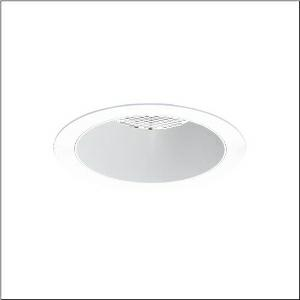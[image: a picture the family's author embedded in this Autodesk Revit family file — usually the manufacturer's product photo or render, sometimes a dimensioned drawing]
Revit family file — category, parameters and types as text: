
# Revit family: lunis_21_xl_51db18mf91c
name_source: partatom
category: Lighting Fixtures
units: mm (PartAtom-declared; Revit-internal decimal feet)

## family parameters
Cut with Voids When Loaded = No
Host = Face
Light Source = No
Part Type = Normal
Room Calculation Point = No
Round Connector Dimension = Use Diameter
Shared = No

## types (1)
- --- (1 x LED, 3700 lm, 21.7 W, 6500K)
    Apparent Load = 22 VA
    CIE Flux Codes = 87 97 99 100 100
    Color Rendering = 80
    Color Temperature = 6500K
    Default Elevation = 1800 mm
    Description = Lunis 21,  XL, downlight, light control with lens, of PMMA, anti glare with reflector, of PC, light emission: direct distribution, LED rated luminous flux: 2.480lm, light colour: 830/840/865, with terminal, 3-pole, mains connection: 220..240V, AC/DC, 0/50..60Hz, housing, round, of diecast aluminium, traffic white (RAL 9016), diameter: 230mm, clamping range: 1..40mm, protection rating (complete): IP20, protection rating (on room side): IP54, insulation class (complete): insulation class II (safety insulation), certification: CE, impact resistance: IK03, packaging unit: 1 piece
    Height = 0 mm  [stored 0 ft]
    Lamp = 1 x LED
    Lamp Light Flux = 3700 lm
    Lamp Power = 21.7 W
    Lamp count = 1
    Length = 230 mm
    Luminous efficacy = 171 lm/W
    Manufacturer = Siteco
    ModVariant = No
    Model = 51DB18MF91C
    Mounting Place = Ceiling
    Mounting Type = Recessed
    Number of Poles = 1
    OnlyDefault = Yes
    Power Factor = 1
    Product Name = Lunis 21 XL
    Product group = downlight
    ProductGroupID = 400
    Protection Class = Protection class II
    Protection Degree = IP 20
    RLX_Detail_Level = 1
    RLX_Emergency_Light_Flux = 0 lm
    RLX_Emergency_Type = 0
    RLX_Emergency_Type_DB = No
    RlxData = <blob elided: 18237 chars, md5=b374e8fa>
    Socket = socket
    Standby Power = 0 W
    System Light Flux = 3700 lm
    System Power = 22 W
    Type Comments = individual setting: colour temperature 6500K, luminous flux: 100 % | (OFF | ON | ON | ON) | 650 mA
    Type Image = l_1291159.jpg
    URL = http://relux.com
    VarID = @adj_019312
    Voltage = 0 V
    Weight = 0.00 kg
    Width = 0 mm  [stored 0 ft]

note: [stored X ft] marks values corroborated as IEEE doubles in the binary element streams (Revit-internal decimal feet)

## geometry (parser evidence)
native form markers: Blend x4, Sweep x12
no freeform markers — native parametric forms only
